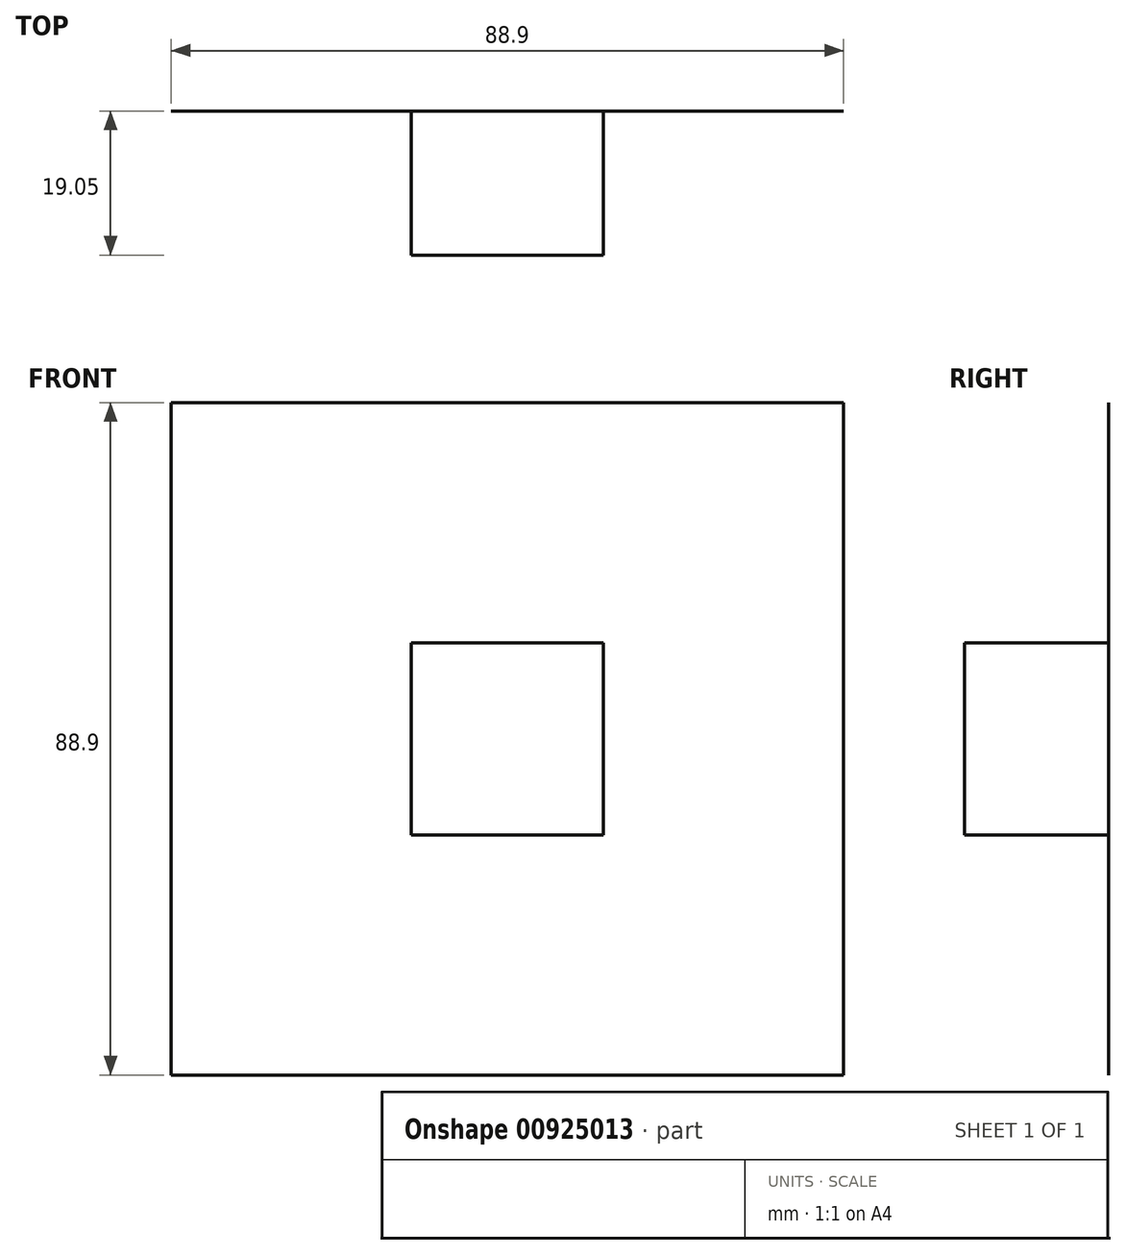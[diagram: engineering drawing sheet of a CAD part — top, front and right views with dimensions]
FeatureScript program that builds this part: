
annotation { "Feature Type Name" : "Feature", "Feature Type Description" : "" }
export const myFeature = defineFeature(function(context is Context, id is Id, definition is map)
    precondition{}
    {
        {
            var Q0;
            Q0=qCreatedBy(makeId("Front.planeOp"),FACE);
            var sketch = newSketch(context, id + "F0", { "sketchPlane" : qUnion([Q0])});
            skLineSegment(sketch, "E0.bottom", {"start": v(0, 0) * mm, "end": v(88.9, 0) * mm});
            skLineSegment(sketch, "E0.top", {"start": v(0, 88.9) * mm, "end": v(88.9, 88.9) * mm});
            skLineSegment(sketch, "E0.left", {"start": v(0, 0) * mm, "end": v(0, 88.9) * mm});
            skLineSegment(sketch, "E0.right", {"start": v(88.9, 0) * mm, "end": v(88.9, 88.9) * mm});
            skLineSegment(sketch, "E1.bottom", {"start": v(31.75, 57.15) * mm, "end": v(57.15, 57.15) * mm});
            skLineSegment(sketch, "E1.top", {"start": v(31.75, 31.75) * mm, "end": v(57.15, 31.75) * mm});
            skLineSegment(sketch, "E1.left", {"start": v(31.75, 57.15) * mm, "end": v(31.75, 31.75) * mm});
            skLineSegment(sketch, "E1.right", {"start": v(57.15, 57.15) * mm, "end": v(57.15, 31.75) * mm});
            skSolve(sketch);
        }
        {
            var Q0;
            Q0=makeQuery(id+"F0.imprint","IMPRINT",FACE,{"disambiguationData":[TD([[makeQuery(id+"F0.imprint","IMPRINT",EDGE,{"derivedFrom":sQuery(id+"F0.wireOp",EDGE,"E0.bottom")}),1.0]])]});
            extrude(context, id + "F1", {"entities" : qUnion([Q0]), "depth" : 5 / 203.2 * mm, "offsetDistance" : 25.4 * mm});
        }
        {
            var Q0;
            Q0=makeQuery(id+"F0.imprint","IMPRINT",FACE,{"disambiguationData":[TD([[makeQuery(id+"F0.imprint","IMPRINT",EDGE,{"derivedFrom":sQuery(id+"F0.wireOp",EDGE,"E1.bottom")}),-1.0]])]});
            extrude(context, id + "F2", {"entities" : qUnion([Q0]), "operationType" : NewBodyOperationType.ADD, "depth" : 19.05 * mm, "offsetDistance" : 25.4 * mm});
        }
    });
